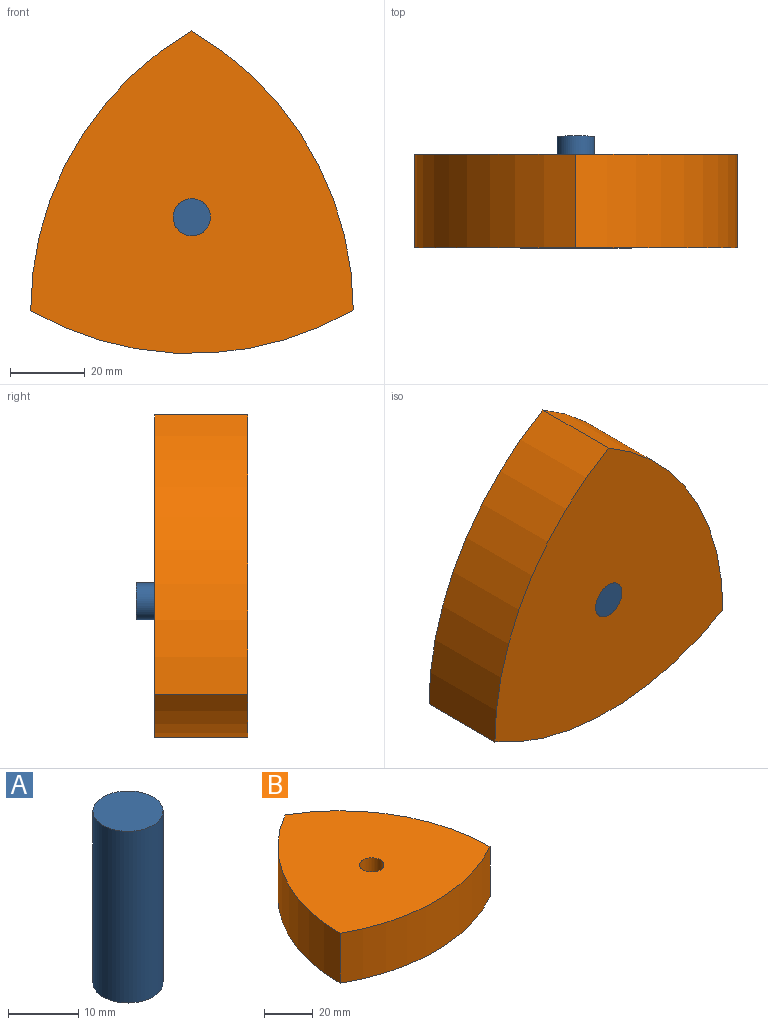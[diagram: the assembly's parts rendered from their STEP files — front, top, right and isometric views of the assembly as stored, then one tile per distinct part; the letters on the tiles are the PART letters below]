
ASSEMBLY  parts=2 mates=1
PART A: 3 faces, bbox 10x10x30 mm
  f0: cylinder r=5mm len=30mm, axis (0,0,-1), area 942.5mm2, adj f1,f2
  f1: plane 10x10mm, normal (0,0,1), area 78.5mm2, adj f0
  f2: plane 10x10mm, normal (0,0,-1), area 78.5mm2, adj f0
PART B: 6 faces, bbox 86.6x86.6x25 mm
  f0: cylinder r=86.6mm len=75mm, axis (0,0,-1), area 2267.2mm2, adj f1,f2,f4,f5
  f1: cylinder r=86.6mm len=75mm, axis (0,0,-1), area 2267.2mm2, adj f0,f2,f4,f5
  f2: cylinder r=86.6mm len=86.6mm, axis (0,0,-1), area 2267.2mm2, adj f0,f1,f4,f5
  f3: cylinder r=5mm len=25mm, axis (0,0,-1), area 785.4mm2, adj f4,f5
  f4: plane 86.6x86.6mm, normal (0,0,1), area 5207.2mm2, adj f0,f1,f2,f3
  f5: plane 86.6x86.6mm, normal (0,0,-1), area 5207.2mm2, adj f0,f1,f2,f3
PLACE A rot(axis=(0,-0.71,0.71),180deg) t=(0,-5,0)mm
PLACE B rot(axis=(0.38,-0.65,0.65),138.7deg) t=(0,-5,0)mm
MATE revolute B.f3 <-> A.f0  axis (0,-1,0) through (0,-30,0)mm
